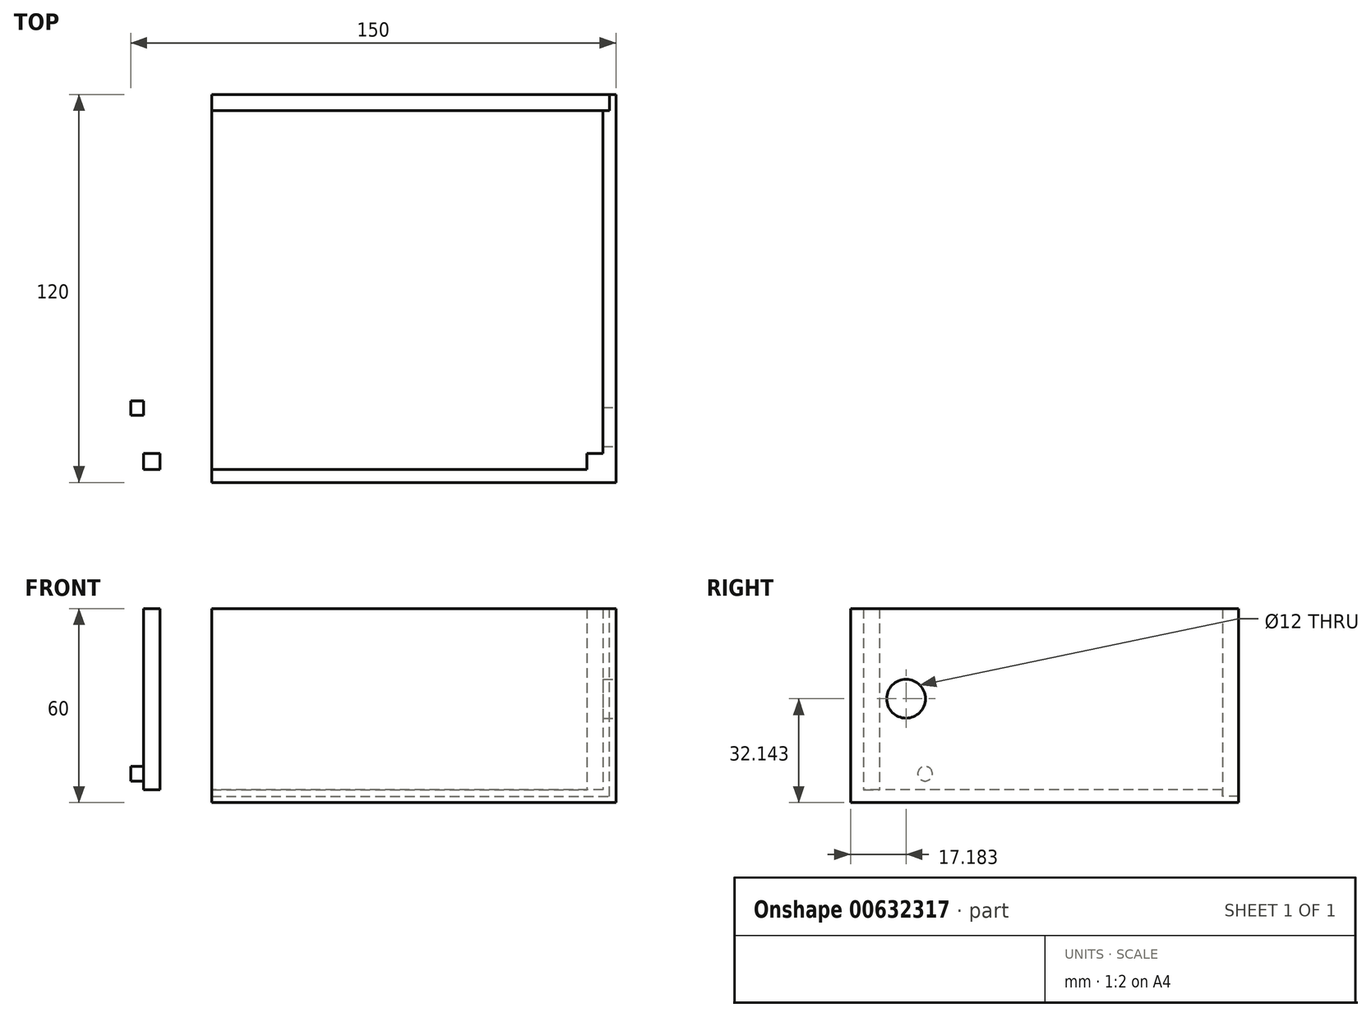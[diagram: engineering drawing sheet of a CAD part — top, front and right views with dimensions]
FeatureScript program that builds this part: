
annotation { "Feature Type Name" : "Feature", "Feature Type Description" : "" }
export const myFeature = defineFeature(function(context is Context, id is Id, definition is map)
    precondition{}
    {
        {
            var Q0;
            Q0=qCreatedBy(makeId("Right.planeOp"),FACE);
            var sketch = newSketch(context, id + "F0", { "sketchPlane" : qUnion([Q0])});
            skLineSegment(sketch, "E0.bottom", {"start": v(0, 0) * mm, "end": v(-120, 0) * mm});
            skLineSegment(sketch, "E0.top", {"start": v(0, 60) * mm, "end": v(-120, 60) * mm});
            skLineSegment(sketch, "E0.left", {"start": v(0, 0) * mm, "end": v(0, 60) * mm});
            skLineSegment(sketch, "E0.right", {"start": v(-120, 0) * mm, "end": v(-120, 60) * mm});
            skCircle(sketch, "E1", {"center": v(-102.82, 32.14) * mm, "radius": 6 * mm});
            skSolve(sketch);
        }
        {
            var Q0;
            Q0=makeQuery(id+"F0.imprint","IMPRINT",FACE,{"disambiguationData":[TD([[makeQuery(id+"F0.imprint","IMPRINT",EDGE,{"derivedFrom":sQuery(id+"F0.wireOp",EDGE,"E0.bottom")}),-1.0]])]});
            var Q1;
            Q1=makeQuery(id+"F0.imprint","IMPRINT",FACE,{"disambiguationData":[TD([[makeQuery(id+"F0.imprint","IMPRINT",EDGE,{"derivedFrom":sQuery(id+"F0.wireOp",EDGE,"E1")}),1.0]])]});
            extrude(context, id + "F1", {"entities" : qUnion([Q0, Q1]), "oppositeDirection" : true, "depth" : 150 * mm, "offsetDistance" : 25 * mm});
        }
        {
            var Q0;
            Q0=makeQuery(id+"F1.opExtrude","SWEPT_FACE",FACE,{"disambiguationData":[OSD([sQuery(id+"F0.wireOp",EDGE,"E0.top")])]});
            var sketch = newSketch(context, id + "F2", { "sketchPlane" : qUnion([Q0])});
            skLineSegment(sketch, "E2.bottom", {"start": v(-146, 0) * mm, "end": v(-4, 0) * mm});
            skLineSegment(sketch, "E2.top", {"start": v(-146, -116) * mm, "end": v(-4, -116) * mm});
            skLineSegment(sketch, "E2.left", {"start": v(-146, 0) * mm, "end": v(-146, -116) * mm});
            skLineSegment(sketch, "E2.right", {"start": v(-4, 0) * mm, "end": v(-4, -116) * mm});
            skSolve(sketch);
        }
        {
            var Q0;
            Q0=makeQuery(id+"F2.imprint","IMPRINT",FACE,{"disambiguationData":[TD([[makeQuery(id+"F2.imprint","IMPRINT",EDGE,{"derivedFrom":sQuery(id+"F2.wireOp",EDGE,"E2.bottom")}),-1.0]])]});
            extrude(context, id + "F3", {"entities" : qUnion([Q0]), "operationType" : NewBodyOperationType.REMOVE, "oppositeDirection" : true, "depth" : 56 * mm, "offsetDistance" : 25 * mm});
        }
        {
            var Q0;
            Q0=makeQuery(id+"F3.boolean.opBoolean","COPY",FACE,{"derivedFrom":makeQuery(id+"F3.opExtrude","SWEPT_FACE",FACE,{"disambiguationData":[OSD([sQuery(id+"F2.wireOp",EDGE,"E2.right")])]})});
            var sketch = newSketch(context, id + "F4", { "sketchPlane" : qUnion([Q0])});
            skLineSegment(sketch, "E3.bottom", {"start": v(0, 60) * mm, "end": v(5, 60) * mm});
            skLineSegment(sketch, "E3.top", {"start": v(0, 4) * mm, "end": v(5, 4) * mm});
            skLineSegment(sketch, "E3.left", {"start": v(0, 60) * mm, "end": v(0, 4) * mm});
            skLineSegment(sketch, "E3.right", {"start": v(5, 60) * mm, "end": v(5, 4) * mm});
            skSolve(sketch);
        }
        {
            var Q0;
            Q0=makeQuery(id+"F4.imprint","IMPRINT",FACE,{"disambiguationData":[TD([[makeQuery(id+"F4.imprint","IMPRINT",EDGE,{"derivedFrom":sQuery(id+"F4.wireOp",EDGE,"E3.bottom")}),-1.0]])]});
            extrude(context, id + "F5", {"entities" : qUnion([Q0]), "operationType" : NewBodyOperationType.REMOVE, "oppositeDirection" : true, "depth" : 2 * mm, "offsetDistance" : 25 * mm});
        }
        {
            var Q0;
            Q0=makeQuery(id+"F3.boolean.opBoolean","COPY",FACE,{"derivedFrom":makeQuery(id+"F3.opExtrude","SWEPT_FACE",FACE,{"disambiguationData":[OSD([sQuery(id+"F2.wireOp",EDGE,"E2.left")])]})});
            var sketch = newSketch(context, id + "F6", { "sketchPlane" : qUnion([Q0])});
            skLineSegment(sketch, "E4.bottom", {"start": v(0, 4) * mm, "end": v(-5, 4) * mm});
            skLineSegment(sketch, "E4.top", {"start": v(0, 60) * mm, "end": v(-5, 60) * mm});
            skLineSegment(sketch, "E4.left", {"start": v(0, 4) * mm, "end": v(0, 60) * mm});
            skLineSegment(sketch, "E4.right", {"start": v(-5, 4) * mm, "end": v(-5, 60) * mm});
            skSolve(sketch);
        }
        {
            var Q0;
            Q0 = qSketchRegion(id + "F6", true);
            extrude(context, id + "F7", {"entities" : qUnion([Q0]), "operationType" : NewBodyOperationType.REMOVE, "oppositeDirection" : true, "depth" : 2 * mm, "offsetDistance" : 25 * mm});
        }
        {
            var Q0;
            Q0=makeQuery(id+"F7.boolean.opBoolean","MERGE",FACE,{"derivedFrom":[makeQuery(id+"F5.boolean.opBoolean","MERGE",FACE,{"derivedFrom":[makeQuery(id+"F3.boolean.opBoolean","COPY",FACE,{"derivedFrom":makeQuery(id+"F3.opExtrude","CAP_FACE",FACE,{"disambiguationData":[OSD([sQuery(id+"F2.wireOp",EDGE,"E2.bottom"),sQuery(id+"F2.wireOp",EDGE,"E2.top"),sQuery(id+"F2.wireOp",EDGE,"E2.left"),sQuery(id+"F2.wireOp",EDGE,"E2.right")])],"isStart":false})}),makeQuery(id+"F5.opExtrude","SWEPT_FACE",FACE,{"disambiguationData":[OSD([sQuery(id+"F4.wireOp",EDGE,"E3.top")])]})]}),makeQuery(id+"F7.opExtrude","SWEPT_FACE",FACE,{"disambiguationData":[OSD([sQuery(id+"F6.wireOp",EDGE,"E4.bottom")])]})]});
            var sketch = newSketch(context, id + "F8", { "sketchPlane" : qUnion([Q0])});
            skLineSegment(sketch, "E5.bottom", {"start": v(-2, -5) * mm, "end": v(-148, -5) * mm});
            skLineSegment(sketch, "E5.top", {"start": v(-2, 0) * mm, "end": v(-148, 0) * mm});
            skLineSegment(sketch, "E5.left", {"start": v(-2, -5) * mm, "end": v(-2, 0) * mm});
            skLineSegment(sketch, "E5.right", {"start": v(-148, -5) * mm, "end": v(-148, 0) * mm});
            skSolve(sketch);
        }
        {
            var Q0;
            Q0=makeQuery(id+"F8.imprint","IMPRINT",FACE,{"disambiguationData":[TD([[makeQuery(id+"F8.imprint","IMPRINT",EDGE,{"derivedFrom":sQuery(id+"F8.wireOp",EDGE,"E5.top")}),-1.0]])]});
            extrude(context, id + "F9", {"entities" : qUnion([Q0]), "operationType" : NewBodyOperationType.REMOVE, "oppositeDirection" : true, "depth" : 2 * mm, "offsetDistance" : 25 * mm});
        }
        {
            var Q0;
            Q0=makeQuery(id+"F1.opExtrude","CAP_FACE",FACE,{"disambiguationData":[OSD([sQuery(id+"F0.wireOp",EDGE,"E0.bottom"),sQuery(id+"F0.wireOp",EDGE,"E0.top"),sQuery(id+"F0.wireOp",EDGE,"E0.left"),sQuery(id+"F0.wireOp",EDGE,"E0.right")])],"isStart":false});
            var sketch = newSketch(context, id + "F10", { "sketchPlane" : qUnion([Q0])});
            skLineSegment(sketch, "E6.bottom", {"start": v(106.44, 43.45) * mm, "end": v(87.44, 43.45) * mm});
            skLineSegment(sketch, "E6.top", {"start": v(106.44, 15.45) * mm, "end": v(87.44, 15.45) * mm});
            skLineSegment(sketch, "E6.left", {"start": v(106.44, 43.45) * mm, "end": v(106.44, 15.45) * mm});
            skLineSegment(sketch, "E6.right", {"start": v(87.44, 43.45) * mm, "end": v(87.44, 15.45) * mm});
            skPoint(sketch, "E7.endSnap0", {"position": v(96.94, 15.45) * mm});
            skPoint(sketch, "E8.endSnap0", {"position": v(96.94, 43.45) * mm});
            skLineSegment(sketch, "E9", {"start": v(87.44, 29.45) * mm, "end": v(106.44, 29.45) * mm, "construction": true});
            skPoint(sketch, "E10.visualSharp", {"position": v(96.94, 57.5) * mm});
            skPoint(sketch, "E11.visualSharp", {"position": v(96.94, 1.39) * mm});
            skCircle(sketch, "E12", {"center": v(96.94, 49.95) * mm, "radius": 2.25 * mm});
            skCircle(sketch, "E13.MirrorC", {"center": v(96.94, 8.95) * mm, "radius": 2.25 * mm});
            skSolve(sketch);
        }
        {
            var Q0;
            Q0=makeQuery(id+"F10.imprint","IMPRINT",FACE,{"disambiguationData":[TD([[makeQuery(id+"F10.imprint","IMPRINT",EDGE,{"derivedFrom":sQuery(id+"F10.wireOp",EDGE,"E12")}),1.0]])]});
            extrude(context, id + "F11", {"entities" : qUnion([Q0]), "operationType" : NewBodyOperationType.REMOVE, "oppositeDirection" : true, "depth" : 11.6 * mm, "offsetDistance" : 25 * mm});
        }
        {
            var Q0;
            Q0=makeQuery(id+"F10.imprint","IMPRINT",FACE,{"disambiguationData":[TD([[makeQuery(id+"F10.imprint","IMPRINT",EDGE,{"derivedFrom":sQuery(id+"F10.wireOp",EDGE,"E6.bottom")}),1.0]])]});
            extrude(context, id + "F12", {"entities" : qUnion([Q0]), "operationType" : NewBodyOperationType.REMOVE, "oppositeDirection" : true, "depth" : 25 * mm, "offsetDistance" : 25 * mm});
        }
        {
            var Q0;
            Q0=makeQuery(id+"F10.imprint","IMPRINT",FACE,{"disambiguationData":[TD([[makeQuery(id+"F10.imprint","IMPRINT",EDGE,{"derivedFrom":sQuery(id+"F10.wireOp",EDGE,"E13.MirrorC")}),-1.0]])]});
            extrude(context, id + "F13", {"entities" : qUnion([Q0]), "operationType" : NewBodyOperationType.REMOVE, "oppositeDirection" : true, "depth" : 25 * mm, "offsetDistance" : 25 * mm});
        }
        {
            var Q0;
            Q0=makeQuery(id+"F7.boolean.opBoolean","MERGE",FACE,{"derivedFrom":[makeQuery(id+"F5.boolean.opBoolean","MERGE",FACE,{"derivedFrom":[makeQuery(id+"F3.boolean.opBoolean","COPY",FACE,{"derivedFrom":makeQuery(id+"F3.opExtrude","CAP_FACE",FACE,{"disambiguationData":[OSD([sQuery(id+"F2.wireOp",EDGE,"E2.bottom"),sQuery(id+"F2.wireOp",EDGE,"E2.top"),sQuery(id+"F2.wireOp",EDGE,"E2.left"),sQuery(id+"F2.wireOp",EDGE,"E2.right")])],"isStart":false})}),makeQuery(id+"F5.opExtrude","SWEPT_FACE",FACE,{"disambiguationData":[OSD([sQuery(id+"F4.wireOp",EDGE,"E3.top")])]})]}),makeQuery(id+"F7.opExtrude","SWEPT_FACE",FACE,{"disambiguationData":[OSD([sQuery(id+"F6.wireOp",EDGE,"E4.bottom")])]})]});
            var sketch = newSketch(context, id + "F14", { "sketchPlane" : qUnion([Q0])});
            skPoint(sketch, "E14.0", {"position": v(-4, -116) * mm});
            skLineSegment(sketch, "E15.bottom", {"start": v(-4, -116) * mm, "end": v(-9, -116) * mm});
            skLineSegment(sketch, "E15.top", {"start": v(-4, -111) * mm, "end": v(-9, -111) * mm});
            skLineSegment(sketch, "E15.left", {"start": v(-4, -116) * mm, "end": v(-4, -111) * mm});
            skLineSegment(sketch, "E15.right", {"start": v(-9, -116) * mm, "end": v(-9, -111) * mm});
            skLineSegment(sketch, "E16.bottom", {"start": v(-146, -116) * mm, "end": v(-141, -116) * mm});
            skLineSegment(sketch, "E16.top", {"start": v(-146, -111) * mm, "end": v(-141, -111) * mm});
            skLineSegment(sketch, "E16.left", {"start": v(-146, -116) * mm, "end": v(-146, -111) * mm});
            skLineSegment(sketch, "E16.right", {"start": v(-141, -116) * mm, "end": v(-141, -111) * mm});
            skSolve(sketch);
        }
        {
            var Q0;
            Q0=makeQuery(id+"F0.imprint","IMPRINT",FACE,{"disambiguationData":[TD([[makeQuery(id+"F0.imprint","IMPRINT",EDGE,{"derivedFrom":sQuery(id+"F0.wireOp",EDGE,"E1")}),1.0]])]});
            extrude(context, id + "F15", {"entities" : qUnion([Q0]), "operationType" : NewBodyOperationType.REMOVE, "oppositeDirection" : true, "depth" : 20 * mm, "offsetDistance" : 25 * mm});
        }
        {
            var Q0;
            Q0=makeQuery(id+"F14.imprint","IMPRINT",FACE,{"disambiguationData":[TD([[makeQuery(id+"F14.imprint","IMPRINT",EDGE,{"derivedFrom":sQuery(id+"F14.wireOp",EDGE,"E15.bottom")}),1.0]])]});
            var Q1;
            Q1=makeQuery(id+"F14.imprint","IMPRINT",FACE,{"disambiguationData":[TD([[makeQuery(id+"F14.imprint","IMPRINT",EDGE,{"derivedFrom":sQuery(id+"F14.wireOp",EDGE,"E16.bottom")}),1.0]])]});
            extrude(context, id + "F16", {"entities" : qUnion([Q0, Q1]), "operationType" : NewBodyOperationType.ADD, "depth" : 56 * mm, "offsetDistance" : 25 * mm});
        }
    });
